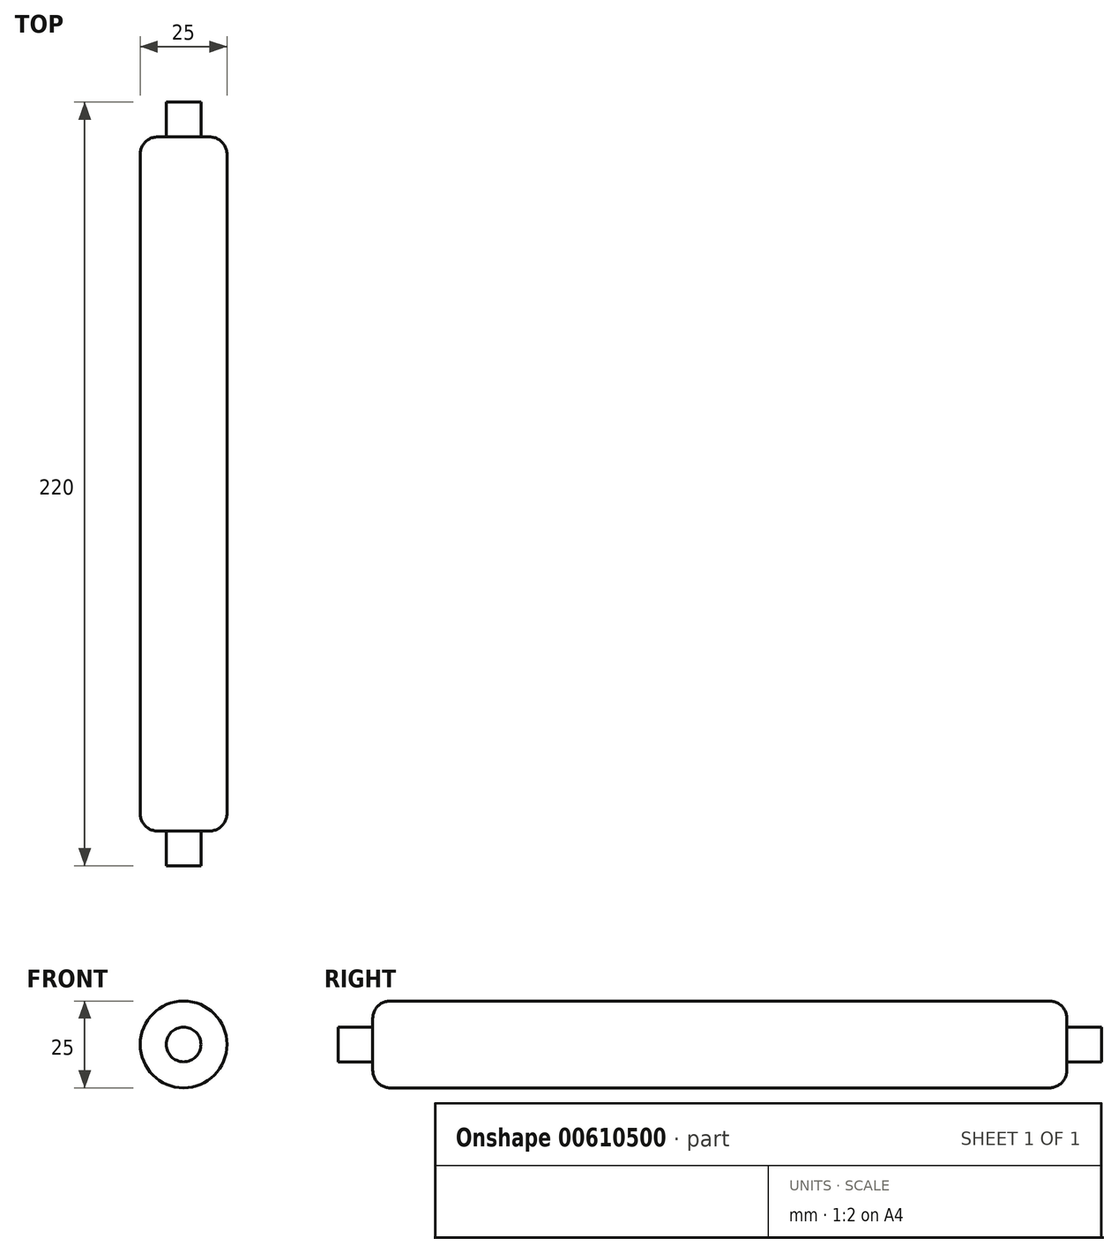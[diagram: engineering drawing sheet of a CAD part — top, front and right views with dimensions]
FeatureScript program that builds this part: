
annotation { "Feature Type Name" : "Feature", "Feature Type Description" : "" }
export const myFeature = defineFeature(function(context is Context, id is Id, definition is map)
    precondition{}
    {
        {
            var Q0;
            Q0=qCreatedBy(makeId("Front.planeOp"),FACE);
            var sketch = newSketch(context, id + "F0", { "sketchPlane" : qUnion([Q0])});
            skCircle(sketch, "E0", {"center": v(0, 0) * mm, "radius": 12.5 * mm});
            skSolve(sketch);
        }
        {
            var Q0;
            Q0=makeQuery(id+"F0.imprint","IMPRINT",FACE,{"disambiguationData":[TD([[makeQuery(id+"F0.imprint","IMPRINT",EDGE,{"derivedFrom":sQuery(id+"F0.wireOp",EDGE,"E0")}),1.0]])]});
            extrude(context, id + "F1", {"entities" : qUnion([Q0]), "depth" : 200 * mm, "offsetDistance" : 25 * mm});
        }
        {
            var Q0;
            Q0=makeQuery(id+"F1.opExtrude","CAP_FACE",FACE,{"disambiguationData":[OSD([sQuery(id+"F0.wireOp",EDGE,"E0")])],"isStart":false});
            var sketch = newSketch(context, id + "F2", { "sketchPlane" : qUnion([Q0])});
            skCircle(sketch, "E1", {"center": v(0, 0) * mm, "radius": 5 * mm});
            skSolve(sketch);
        }
        {
            var Q0;
            Q0=makeQuery(id+"F2.imprint","IMPRINT",FACE,{"disambiguationData":[TD([[makeQuery(id+"F2.imprint","IMPRINT",EDGE,{"derivedFrom":sQuery(id+"F2.wireOp",EDGE,"E1")}),1.0]])]});
            extrude(context, id + "F3", {"entities" : qUnion([Q0]), "operationType" : NewBodyOperationType.ADD, "depth" : 10 * mm, "offsetDistance" : 25 * mm});
        }
        {
            var Q0;
            Q0=makeQuery(id+"F1.opExtrude","CAP_FACE",FACE,{"disambiguationData":[OSD([sQuery(id+"F0.wireOp",EDGE,"E0")])],"isStart":true});
            var sketch = newSketch(context, id + "F4", { "sketchPlane" : qUnion([Q0])});
            skCircle(sketch, "E2", {"center": v(0, 0) * mm, "radius": 5 * mm});
            skSolve(sketch);
        }
        {
            var Q0;
            Q0=makeQuery(id+"F4.imprint","IMPRINT",FACE,{"disambiguationData":[TD([[makeQuery(id+"F4.imprint","IMPRINT",EDGE,{"derivedFrom":sQuery(id+"F4.wireOp",EDGE,"E2")}),1.0]])]});
            extrude(context, id + "F5", {"entities" : qUnion([Q0]), "operationType" : NewBodyOperationType.ADD, "depth" : 10 * mm, "offsetDistance" : 25 * mm});
        }
        {
            var Q0;
            Q0=makeQuery(id+"F1.opExtrude","CAP_EDGE",EDGE,{"disambiguationData":[OSD([sQuery(id+"F0.wireOp",EDGE,"E0")])],"isStart":false});
            fillet(context, id + "F6", {"entities" : qUnion([Q0]), "radius" : 5 * mm, "tangentPropagation" : true, "allowEdgeOverflow" : false});
        }
        {
            var Q0;
            Q0=makeQuery(id+"F1.opExtrude","CAP_EDGE",EDGE,{"disambiguationData":[OSD([sQuery(id+"F0.wireOp",EDGE,"E0")])],"isStart":true});
            var Q1;
            Q1=makeQuery(id+"F6.opFillet","BLEND_FACE",FACE,{"disambiguationData":[OSD([sQuery(id+"F0.wireOp",EDGE,"E0")])]});
            fillet(context, id + "F7", {"entities" : qUnion([Q0, Q1]), "radius" : 5 * mm, "tangentPropagation" : true, "allowEdgeOverflow" : false});
        }
    });
